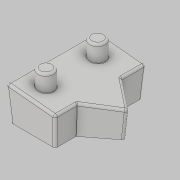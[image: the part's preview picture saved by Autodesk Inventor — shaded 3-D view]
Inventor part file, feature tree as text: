
AUTODESK INVENTOR PART (.ipt)
format: ipt  version: 2019 (Build 230136000, 136)  size: 278,016 bytes
history: native  units: mm
features: extrude x3, sketch x3, draft x1, fillet x1, shell x1
ambient origin geometry x8: Origin, YZ Plane, XZ Plane, XY Plane, X Axis, Y Axis, Z Axis, Center Point
bodies: Solid1 (feature_tree)
feature tree (9):
  extrude  "Extrusion1"  Depth=200.0mm
  extrude  "Extrusion2"  Depth=42.0mm
  extrude  "Extrusion3"  TaperAngle=75.0deg  [1 undecoded]
  draft  "FaceDraft1"
  fillet  "Fillet1"  Radius=52.0mm
  shell  "Shell2"  Thickness=110.0mm
  sketch  "Sketch1"  dims[d0=100.0mm d1=200.0mm]
  sketch  "Sketch2"  dims[d2=35.0mm d4=42.0mm]
  sketch  "Sketch3"  dims[d5=42.0mm d6=75.0deg d7=52.0mm d8=110.0mm d9=0.0mm d11=62.0mm d12=77.0mm d13=110.0mm d14=0.0mm d22=110.0mm d23=0.0mm d25=0.698132mm d26=5.0mm d27=1.0mm d28=4.0mm]
note: 1 required parameter value undecoded (feature->parameter linkage not recoverable at this tier; creation-order binding heuristic only, values carry confidence <= 0.55)
